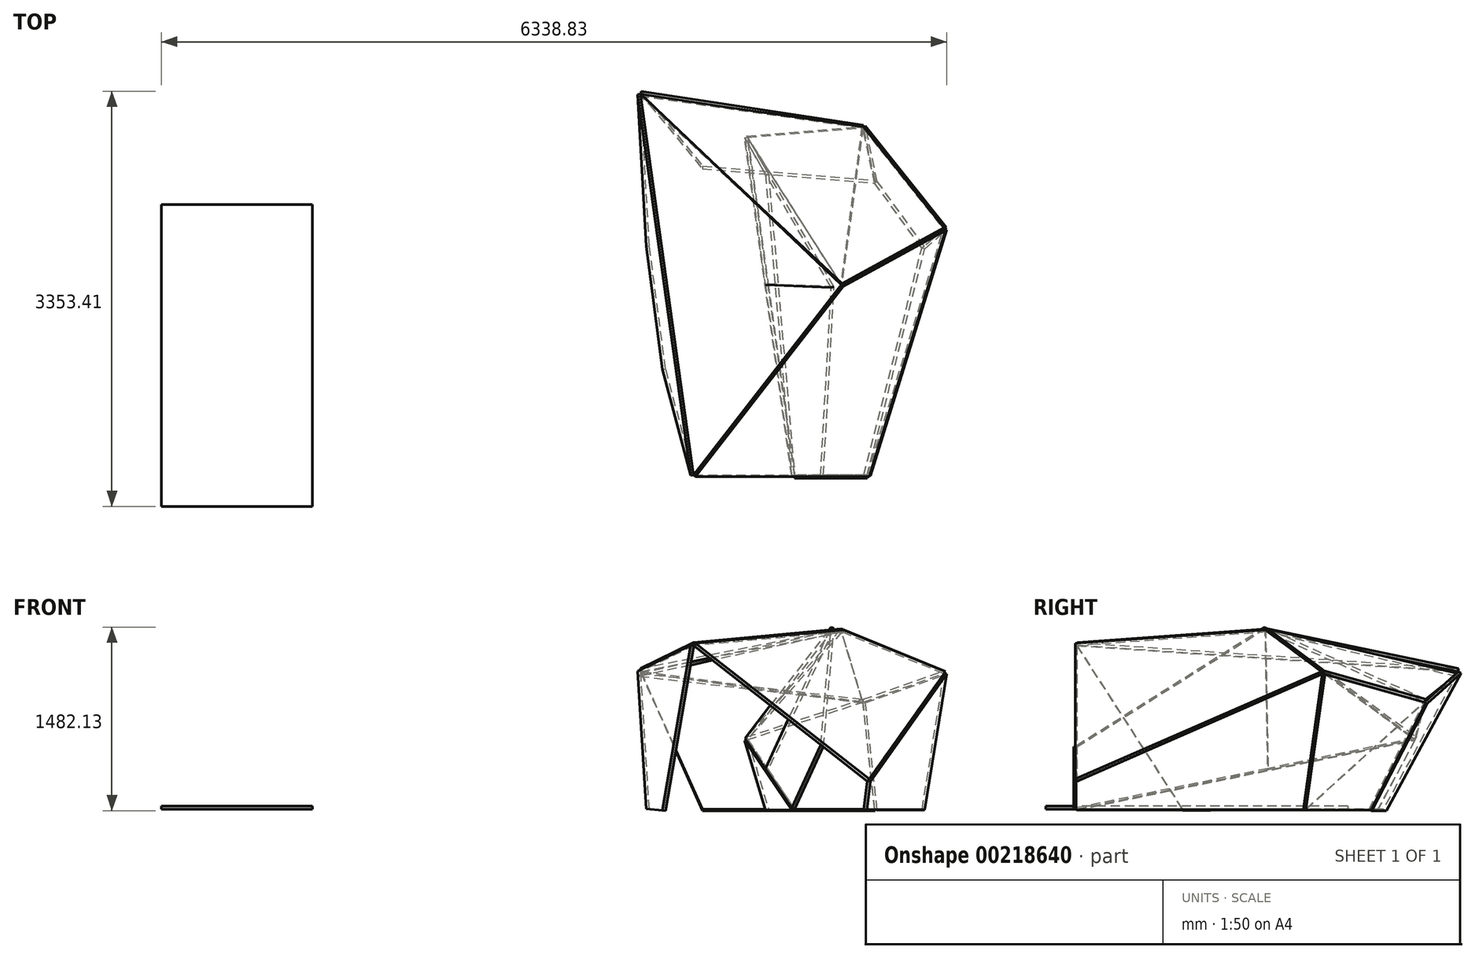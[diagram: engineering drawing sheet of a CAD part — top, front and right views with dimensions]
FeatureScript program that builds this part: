
annotation { "Feature Type Name" : "Feature", "Feature Type Description" : "" }
export const myFeature = defineFeature(function(context is Context, id is Id, definition is map)
    precondition{}
    {
        {
            var Q0;
            Q0=qCreatedBy(makeId("Top.planeOp"),FACE);
            var sketch = newSketch(context, id + "F0", { "sketchPlane" : qUnion([Q0])});
            skLineSegment(sketch, "E0", {"start": v(8.88, 54.26) * mm, "end": v(284.61, 9.14) * mm, "construction": true});
            skLineSegment(sketch, "E1", {"start": v(346.15, 1800.72) * mm, "end": v(521.62, 1772) * mm, "construction": true});
            skLineSegment(sketch, "E2", {"start": v(521.62, 1772) * mm, "end": v(634.56, 1418.93) * mm, "construction": true});
            skLineSegment(sketch, "E3", {"start": v(8.88, 54.26) * mm, "end": v(126.56, 1502.06) * mm, "construction": true});
            skLineSegment(sketch, "E4", {"start": v(126.56, 1502.06) * mm, "end": v(346.15, 1800.72) * mm, "construction": true});
            skLineSegment(sketch, "E5.MirrorCS", {"start": v(-41.92, 1832.26) * mm, "end": v(-219.72, 1832.26) * mm, "construction": true});
            skLineSegment(sketch, "E6.MirrorCS", {"start": v(8.88, 54.26) * mm, "end": v(-270.52, 54.26) * mm, "construction": true});
            skLineSegment(sketch, "E7.MirrorCS", {"start": v(-219.72, 1832.26) * mm, "end": v(-388.2, 1502.06) * mm, "construction": true});
            skLineSegment(sketch, "E8.MirrorCS", {"start": v(-388.2, 1502.06) * mm, "end": v(-270.52, 54.26) * mm, "construction": true});
            skLineSegment(sketch, "E9.MirrorCS", {"start": v(126.56, 1502.06) * mm, "end": v(-41.92, 1832.26) * mm, "construction": true});
            skLineSegment(sketch, "E10", {"start": v(279.4, 0) * mm, "end": v(746.99, 1833.49) * mm});
            skLineSegment(sketch, "E11", {"start": v(746.99, 1833.49) * mm, "end": v(367.61, 2358.04) * mm});
            skLineSegment(sketch, "E12", {"start": v(367.61, 2358.04) * mm, "end": v(-489.7, 2429.31) * mm});
            skLineSegment(sketch, "E13", {"start": v(-489.7, 2429.31) * mm, "end": v(-1023.63, 2473.7) * mm});
            skLineSegment(sketch, "E14", {"start": v(-279.4, 0) * mm, "end": v(-489.7, 2429.31) * mm});
            skLineSegment(sketch, "E15", {"start": v(-1023.63, 2473.7) * mm, "end": v(-1452.84, 1852.47) * mm, "construction": true});
            skLineSegment(sketch, "E16", {"start": v(-1452.84, 1852.47) * mm, "end": v(-1440.64, 1029.28) * mm, "construction": true});
            skLineSegment(sketch, "E17", {"start": v(284.61, 9.14) * mm, "end": v(634.56, 1418.93) * mm, "construction": true});
            skLineSegment(sketch, "E18", {"start": v(-279.4, 0) * mm, "end": v(279.4, 0) * mm});
            skLineSegment(sketch, "E19", {"start": v(634.56, 1418.93) * mm, "end": v(126.56, 1502.06) * mm, "construction": true});
            skLineSegment(sketch, "E20", {"start": v(-388.2, 1502.06) * mm, "end": v(126.56, 1502.06) * mm, "construction": true});
            skLineSegment(sketch, "E21", {"start": v(380.56, 1460.5) * mm, "end": v(146.75, 31.7) * mm, "construction": true});
            skLineSegment(sketch, "E22", {"start": v(-130.82, 54.26) * mm, "end": v(-130.82, 1502.06) * mm, "construction": true});
            skLineSegment(sketch, "E23", {"start": v(-130.82, 1502.06) * mm, "end": v(-130.82, 1832.26) * mm, "construction": true});
            skLineSegment(sketch, "E24", {"start": v(-438.93, 1842.81) * mm, "end": v(749.37, 1842.81) * mm, "construction": true});
            skSolve(sketch);
        }
        {
            var Q0;
            Q0=qCreatedBy(makeId("Front.planeOp"),FACE);
            var sketch = newSketch(context, id + "F1", { "sketchPlane" : qUnion([Q0])});
            skLineSegment(sketch, "E25", {"start": v(279.4, 0) * mm, "end": v(307.88, 226.82) * mm});
            skLineSegment(sketch, "E26", {"start": v(307.88, 226.82) * mm, "end": v(-1093.72, 1320.8) * mm});
            skLineSegment(sketch, "E27", {"start": v(279.4, 0) * mm, "end": v(-279.4, 0) * mm});
            skLineSegment(sketch, "E28", {"start": v(-279.4, 0) * mm, "end": v(-46.85, 503.7) * mm});
            skSolve(sketch);
        }
        {
            var Q0;
            Q0=sQuery(id+"F1.wireOp",VERTEX,"E26.start");
            var Q1;
            Q1=sQuery(id+"F1.wireOp",VERTEX,"E25.start");
            var Q2;
            Q2=sQuery(id+"F0.wireOp",VERTEX,"E11.start");
            cPlane(context, id + "F2", {"entities" : qUnion([Q0, Q1, Q2]), "cplaneType" : CPlaneType.THREE_POINT, "offset" : 25.4 * mm, "width" : 152.4 * mm, "height" : 152.4 * mm});
        }
        {
            var Q0;
            Q0=qCreatedBy(id+"F2.planeOp",FACE);
            var sketch = newSketch(context, id + "F3", { "sketchPlane" : qUnion([Q0])});
            skLineSegment(sketch, "E29", {"start": v(-1959.28, 93.07) * mm, "end": v(-2117.8, 1201.52) * mm});
            skLineSegment(sketch, "E30", {"start": v(-2117.8, 1201.52) * mm, "end": v(-68, 263.41) * mm});
            skLineSegment(sketch, "E31", {"start": v(-68, 263.41) * mm, "end": v(-68, 34.81) * mm});
            skLineSegment(sketch, "E32", {"start": v(-68, 34.81) * mm, "end": v(-1959.28, 93.07) * mm});
            skSolve(sketch);
        }
        {
            var Q0;
            Q0=sQuery(id+"F3.wireOp",VERTEX,"E31.start");
            var Q1;
            Q1=sQuery(id+"F3.wireOp",VERTEX,"E30.start");
            var Q2;
            Q2=sQuery(id+"F1.wireOp",VERTEX,"E26.end");
            cPlane(context, id + "F4", {"entities" : qUnion([Q0, Q1, Q2]), "cplaneType" : CPlaneType.THREE_POINT, "offset" : 25.4 * mm, "width" : 152.4 * mm, "height" : 152.4 * mm});
        }
        {
            var Q0;
            Q0=qCreatedBy(id+"F4.planeOp",FACE);
            var sketch = newSketch(context, id + "F5", { "sketchPlane" : qUnion([Q0])});
            skLineSegment(sketch, "E33", {"start": v(156.82, -127.38) * mm, "end": v(889.87, -2259.12) * mm});
            skLineSegment(sketch, "E34", {"start": v(889.87, -2259.12) * mm, "end": v(-89.33, -2075.22) * mm});
            skLineSegment(sketch, "E35", {"start": v(-89.33, -2075.22) * mm, "end": v(-1511.65, -741.77) * mm});
            skLineSegment(sketch, "E36", {"start": v(-1511.65, -741.77) * mm, "end": v(156.82, -127.38) * mm});
            skSolve(sketch);
        }
        {
            var Q0;
            Q0=sQuery(id+"F0.wireOp",VERTEX,"E11.end");
            var Q1;
            Q1=sQuery(id+"F3.wireOp",VERTEX,"E29.start");
            var Q2;
            Q2=sQuery(id+"F5.wireOp",VERTEX,"E34.start");
            cPlane(context, id + "F6", {"entities" : qUnion([Q0, Q1, Q2]), "cplaneType" : CPlaneType.THREE_POINT, "offset" : 25.4 * mm, "width" : 152.4 * mm, "height" : 152.4 * mm});
        }
        {
            var Q0;
            Q0=qCreatedBy(id+"F6.planeOp",FACE);
            var sketch = newSketch(context, id + "F7", { "sketchPlane" : qUnion([Q0])});
            skLineSegment(sketch, "E37", {"start": v(1088.33, 189.9) * mm, "end": v(1728.47, 93.46) * mm});
            skLineSegment(sketch, "E38", {"start": v(1728.47, 93.46) * mm, "end": v(2273.09, 905.47) * mm});
            skLineSegment(sketch, "E39", {"start": v(2273.09, 905.47) * mm, "end": v(1275.86, 1293.82) * mm});
            skLineSegment(sketch, "E40", {"start": v(1275.86, 1293.82) * mm, "end": v(1088.33, 189.9) * mm});
            skSolve(sketch);
        }
        {
            var Q0;
            Q0=sQuery(id+"F0.wireOp",VERTEX,"E13.end");
            var Q1;
            Q1=sQuery(id+"F7.wireOp",VERTEX,"E39.start");
            var Q2;
            Q2=sQuery(id+"F7.wireOp",VERTEX,"E38.start");
            cPlane(context, id + "F8", {"entities" : qUnion([Q0, Q1, Q2]), "cplaneType" : CPlaneType.THREE_POINT, "offset" : 25.4 * mm, "width" : 152.4 * mm, "height" : 152.4 * mm});
        }
        {
            var Q0;
            Q0=qCreatedBy(id+"F8.planeOp",FACE);
            var sketch = newSketch(context, id + "F9", { "sketchPlane" : qUnion([Q0])});
            skLineSegment(sketch, "E41", {"start": v(-1184, 1118.5) * mm, "end": v(211.07, 1066.2) * mm});
            skLineSegment(sketch, "E42", {"start": v(211.07, 1066.2) * mm, "end": v(115.33, 2039.24) * mm});
            skLineSegment(sketch, "E43", {"start": v(115.33, 2039.24) * mm, "end": v(-1683.4, 2383.5) * mm});
            skLineSegment(sketch, "E44", {"start": v(-1683.4, 2383.5) * mm, "end": v(-1184, 1118.5) * mm});
            skLineSegment(sketch, "E45", {"start": v(-648.6, 1098.43) * mm, "end": v(-818.37, 1735.35) * mm});
            skSolve(sketch);
        }
        {
            var Q0;
            Q0=sQuery(id+"F0.wireOp",VERTEX,"E14.start");
            var Q1;
            Q1=sQuery(id+"F0.wireOp",VERTEX,"E12.end");
            var Q2;
            Q2=sQuery(id+"F9.wireOp",VERTEX,"E45.end");
            cPlane(context, id + "F10", {"entities" : qUnion([Q0, Q1, Q2]), "cplaneType" : CPlaneType.THREE_POINT, "offset" : 25.4 * mm, "width" : 152.4 * mm, "height" : 152.4 * mm});
        }
        {
            var Q0;
            Q0=qCreatedBy(id+"F10.planeOp",FACE);
            var sketch = newSketch(context, id + "F11", { "sketchPlane" : qUnion([Q0])});
            skLineSegment(sketch, "E46", {"start": v(-2460.48, 121) * mm, "end": v(-22.63, 69.03) * mm});
            skLineSegment(sketch, "E47", {"start": v(-22.63, 69.03) * mm, "end": v(-2760.72, 707.8) * mm});
            skLineSegment(sketch, "E48", {"start": v(-2760.72, 707.8) * mm, "end": v(-2460.48, 121) * mm});
            skSolve(sketch);
        }
        {
            var Q0;
            Q0=sQuery(id+"F1.wireOp",VERTEX,"E28.end");
            var Q1;
            Q1=sQuery(id+"F0.wireOp",VERTEX,"E14.start");
            var Q2;
            Q2=sQuery(id+"F11.wireOp",VERTEX,"E48.start");
            cPlane(context, id + "F12", {"entities" : qUnion([Q0, Q1, Q2]), "cplaneType" : CPlaneType.THREE_POINT, "offset" : 25.4 * mm, "width" : 152.4 * mm, "height" : 152.4 * mm});
        }
        {
            var Q0;
            Q0=qCreatedBy(id+"F12.planeOp",FACE);
            var sketch = newSketch(context, id + "F13", { "sketchPlane" : qUnion([Q0])});
            skLineSegment(sketch, "E49", {"start": v(-2842.33, 234.4) * mm, "end": v(-52.78, -117.11) * mm});
            skLineSegment(sketch, "E50", {"start": v(-52.78, -117.11) * mm, "end": v(-52.78, 437.67) * mm});
            skLineSegment(sketch, "E51", {"start": v(-52.78, 437.67) * mm, "end": v(-1608.75, 1341.8) * mm});
            skLineSegment(sketch, "E52", {"start": v(-1608.75, 1341.8) * mm, "end": v(-2842.33, 234.4) * mm});
            skLineSegment(sketch, "E53", {"start": v(-1608.75, 1341.8) * mm, "end": v(-1630.58, 81.7) * mm});
            skSolve(sketch);
        }
        {
            var Q0;
            Q0=sQuery(id+"F9.wireOp",VERTEX,"E43.start");
            var Q1;
            Q1=sQuery(id+"F5.wireOp",VERTEX,"E34.start");
            var Q2;
            Q2=sQuery(id+"F5.wireOp",VERTEX,"E35.start");
            cPlane(context, id + "F14", {"entities" : qUnion([Q0, Q1, Q2]), "cplaneType" : CPlaneType.THREE_POINT, "offset" : 25.4 * mm, "width" : 152.4 * mm, "height" : 152.4 * mm});
        }
        {
            var Q0;
            Q0=qCreatedBy(id+"F14.planeOp",FACE);
            var sketch = newSketch(context, id + "F15", { "sketchPlane" : qUnion([Q0])});
            skLineSegment(sketch, "E54", {"start": v(-208.8, 857.64) * mm, "end": v(-1859.73, 2402.3) * mm});
            skLineSegment(sketch, "E55", {"start": v(-1859.73, 2402.3) * mm, "end": v(-35.5, 2245.86) * mm});
            skLineSegment(sketch, "E56", {"start": v(-35.5, 2245.86) * mm, "end": v(624.64, 1403.55) * mm});
            skLineSegment(sketch, "E57", {"start": v(624.64, 1403.55) * mm, "end": v(-208.8, 857.64) * mm});
            skSolve(sketch);
        }
        {
            var Q0;
            Q0 = qSketchRegion(id + "F1", true);
            extrude(context, id + "F16", {"entities" : qUnion([Q0]), "depth" : 25.4 * mm});
        }
        {
            var Q0;
            Q0 = qSketchRegion(id + "F3", true);
            extrude(context, id + "F17", {"entities" : qUnion([Q0]), "oppositeDirection" : true, "depth" : 25.4 * mm});
        }
        {
            var Q0;
            Q0 = qSketchRegion(id + "F5", true);
            extrude(context, id + "F18", {"entities" : qUnion([Q0]), "oppositeDirection" : true, "depth" : 25.4 * mm});
        }
        {
            var Q0;
            Q0 = qSketchRegion(id + "F7", true);
            extrude(context, id + "F19", {"entities" : qUnion([Q0]), "depth" : 25.4 * mm});
        }
        {
            var Q0;
            Q0 = qSketchRegion(id + "F9", true);
            extrude(context, id + "F20", {"entities" : qUnion([Q0]), "oppositeDirection" : true, "depth" : 25.4 * mm});
        }
        {
            var Q0;
            Q0 = qSketchRegion(id + "F11", true);
            extrude(context, id + "F21", {"entities" : qUnion([Q0]), "depth" : 25.4 * mm});
        }
        {
            var Q0;
            {var subQ0=sQuery(id+"F13.wireOp",EDGE,"E52");Q0=makeQuery(id+"F13.imprint","IMPRINT",FACE,{"disambiguationData":[TD([[makeQuery(id+"F13.imprint","IMPRINT",EDGE,{"derivedFrom":subQ0}),1.0]])]});}
            extrude(context, id + "F22", {"entities" : qUnion([Q0]), "depth" : 25.4 * mm});
        }
        {
            var Q0;
            Q0 = qSketchRegion(id + "F15", true);
            extrude(context, id + "F23", {"entities" : qUnion([Q0]), "depth" : 25.4 * mm});
        }
        {
            var Q0;
            Q0=sQuery(id+"F7.wireOp",VERTEX,"E39.start");
            var Q1;
            Q1=sQuery(id+"F5.wireOp",VERTEX,"E35.start");
            var Q2;
            Q2=sQuery(id+"F13.wireOp",VERTEX,"E49.start");
            cPlane(context, id + "F24", {"entities" : qUnion([Q0, Q1, Q2]), "cplaneType" : CPlaneType.THREE_POINT, "offset" : 25.4 * mm, "width" : 152.4 * mm, "height" : 152.4 * mm});
        }
        {
            var Q0;
            Q0=qCreatedBy(id+"F24.planeOp",FACE);
            var sketch = newSketch(context, id + "F25", { "sketchPlane" : qUnion([Q0])});
            skLineSegment(sketch, "E58", {"start": v(-92.9, 2194.2) * mm, "end": v(886.77, 2127.78) * mm});
            skLineSegment(sketch, "E59", {"start": v(886.77, 2127.78) * mm, "end": v(706.82, 740.4) * mm});
            skLineSegment(sketch, "E60", {"start": v(706.82, 740.4) * mm, "end": v(-92.9, 2194.2) * mm});
            skSolve(sketch);
        }
        {
            var Q0;
            Q0 = qSketchRegion(id + "F25", true);
            extrude(context, id + "F26", {"entities" : qUnion([Q0]), "depth" : 25.4 * mm});
        }
        {
            var Q0;
            Q0=sQuery(id+"F5.wireOp",VERTEX,"E35.start");
            var Q1;
            Q1=sQuery(id+"F5.wireOp",VERTEX,"E36.start");
            var Q2;
            Q2=sQuery(id+"F9.wireOp",VERTEX,"E44.start");
            cPlane(context, id + "F27", {"entities" : qUnion([Q0, Q1, Q2]), "cplaneType" : CPlaneType.THREE_POINT, "offset" : 25.4 * mm, "width" : 152.4 * mm, "height" : 152.4 * mm});
        }
        {
            var Q0;
            Q0=qCreatedBy(id+"F27.planeOp",FACE);
            var sketch = newSketch(context, id + "F28", { "sketchPlane" : qUnion([Q0])});
            skLineSegment(sketch, "E61", {"start": v(326.12, 1468.14) * mm, "end": v(-882.49, -61.68) * mm});
            skLineSegment(sketch, "E62", {"start": v(-882.49, -61.68) * mm, "end": v(-1315.38, 3023.35) * mm});
            skLineSegment(sketch, "E63", {"start": v(-1315.38, 3023.35) * mm, "end": v(326.12, 1468.14) * mm});
            skSolve(sketch);
        }
        {
            var Q0;
            Q0=sQuery(id+"F28.wireOp",VERTEX,"E63.start");
            var Q1;
            Q1=sQuery(id+"F28.wireOp",VERTEX,"E62.start");
            var Q2;
            Q2=sQuery(id+"F0.wireOp",VERTEX,"E16.start");
            cPlane(context, id + "F29", {"entities" : qUnion([Q0, Q1, Q2]), "cplaneType" : CPlaneType.THREE_POINT, "offset" : 25.4 * mm, "width" : 152.4 * mm, "height" : 152.4 * mm});
        }
        {
            var Q0;
            Q0=qCreatedBy(id+"F29.planeOp",FACE);
            var sketch = newSketch(context, id + "F30", { "sketchPlane" : qUnion([Q0])});
            skLineSegment(sketch, "E64", {"start": v(-2026.86, -123.1) * mm, "end": v(-3263.76, 978.67) * mm});
            skLineSegment(sketch, "E65", {"start": v(-3263.76, 978.67) * mm, "end": v(-158.14, 1223.38) * mm});
            skLineSegment(sketch, "E66", {"start": v(-158.14, 1223.38) * mm, "end": v(-1024.64, -123.1) * mm});
            skLineSegment(sketch, "E67", {"start": v(-1024.64, -123.1) * mm, "end": v(-2026.86, -123.1) * mm});
            skSolve(sketch);
        }
        {
            var Q0;
            Q0=makeQuery(id+"F28.imprint","IMPRINT",FACE,{"disambiguationData":[TD([[makeQuery(id+"F28.imprint","IMPRINT",EDGE,{"derivedFrom":sQuery(id+"F28.wireOp",EDGE,"E61")}),-1.0]])]});
            extrude(context, id + "F31", {"entities" : qUnion([Q0]), "depth" : 25.4 * mm});
        }
        {
            var Q0;
            Q0=makeQuery(id+"F30.imprint","IMPRINT",FACE,{"disambiguationData":[TD([[makeQuery(id+"F30.imprint","IMPRINT",EDGE,{"derivedFrom":sQuery(id+"F30.wireOp",EDGE,"E64")}),-1.0]])]});
            extrude(context, id + "F32", {"entities" : qUnion([Q0]), "depth" : 25.4 * mm});
        }
        {
            var Q0;
            Q0=qCreatedBy(makeId("Top.planeOp"),FACE);
            var sketch = newSketch(context, id + "F33", { "sketchPlane" : qUnion([Q0])});
            skLineSegment(sketch, "E68.bottom", {"start": v(-5390.72, 2186.2) * mm, "end": v(-4171.52, 2186.2) * mm});
            skLineSegment(sketch, "E68.top", {"start": v(-5390.72, -252.2) * mm, "end": v(-4171.52, -252.2) * mm});
            skLineSegment(sketch, "E68.left", {"start": v(-5390.72, 2186.2) * mm, "end": v(-5390.72, -252.2) * mm});
            skLineSegment(sketch, "E68.right", {"start": v(-4171.52, 2186.2) * mm, "end": v(-4171.52, -252.2) * mm});
            skSolve(sketch);
        }
        {
            var Q0;
            Q0=makeQuery(id+"F33.imprint","IMPRINT",FACE,{"disambiguationData":[TD([[makeQuery(id+"F33.imprint","IMPRINT",EDGE,{"derivedFrom":sQuery(id+"F33.wireOp",EDGE,"E68.bottom")}),-1.0]])]});
            extrude(context, id + "F34", {"entities" : qUnion([Q0]), "depth" : 25.4 * mm});
        }
        {
            var Q0;
            {var subQ0=sQuery(id+"F13.wireOp",EDGE,"E50");Q0=makeQuery(id+"F13.imprint","IMPRINT",FACE,{"disambiguationData":[TD([[makeQuery(id+"F13.imprint","IMPRINT",EDGE,{"derivedFrom":subQ0}),1.0]])]});}
            extrude(context, id + "F35", {"entities" : qUnion([Q0]), "depth" : 25.4 * mm});
        }
    });
